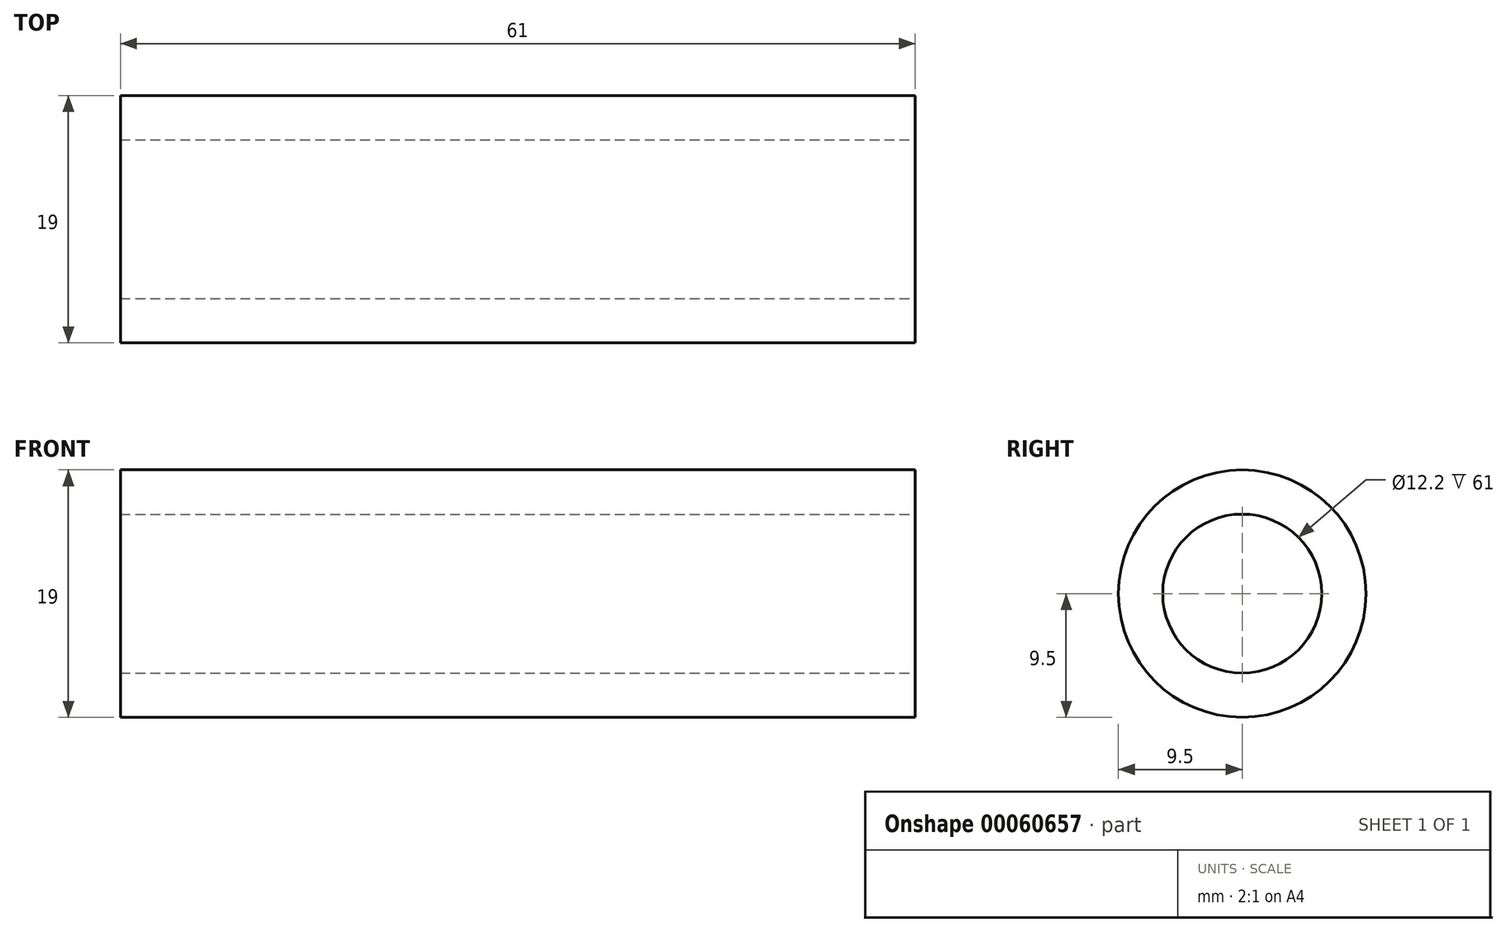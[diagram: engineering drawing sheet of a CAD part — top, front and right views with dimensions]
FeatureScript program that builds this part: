
annotation { "Feature Type Name" : "Feature", "Feature Type Description" : "" }
export const myFeature = defineFeature(function(context is Context, id is Id, definition is map)
    precondition{}
    {
        {
            var Q0;
            Q0=qCreatedBy(makeId("Right.planeOp"),FACE);
            var sketch = newSketch(context, id + "F0", { "sketchPlane" : qUnion([Q0])});
            skCircle(sketch, "E0", {"center": v(0, 0) * mm, "radius": 9.5 * mm});
            skCircle(sketch, "E1", {"center": v(0, 0) * mm, "radius": 6.1 * mm});
            skSolve(sketch);
        }
        {
            var Q0;
            Q0=makeQuery(id+"F0.imprint","IMPRINT",FACE,{"disambiguationData":[TD([[makeQuery(id+"F0.imprint","IMPRINT",EDGE,{"derivedFrom":sQuery(id+"F0.wireOp",EDGE,"E0")}),1.0]])]});
            extrude(context, id + "F1", {"entities" : qUnion([Q0]), "oppositeDirection" : true, "depth" : 61 * mm});
        }
    });
